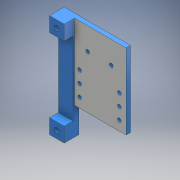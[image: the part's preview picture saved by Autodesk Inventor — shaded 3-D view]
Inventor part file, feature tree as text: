
AUTODESK INVENTOR PART (.ipt)
format: ipt  version: 2018 (Build 220112000, 112)  size: 184,832 bytes
history: native  units: mm
features: sketch x6, extrude x3, hole x3
ambient origin geometry x8: Origin, YZ Plane, XZ Plane, XY Plane, X Axis, Y Axis, Z Axis, Center Point
bodies: Solide1 (feature_tree)
feature tree (12):
  extrude  "Extrusion1"  Depth=25.0mm
  extrude  "Extrusion3"  Depth=35.0mm
  extrude  "Extrusion6"  Depth=10.0mm
  hole  "Perçage1"  [1 undecoded]
  sketch  "Esquisse9"
  hole  "Perçage2"  [1 undecoded]
  hole  "Perçage5"  [1 undecoded]
  sketch  "Esquisse1"
  sketch  "Esquisse3"
  sketch  "Esquisse7"
  sketch  "Esquisse8"
  sketch  "Esquisse18"
note: 3 required parameter values undecoded (feature->parameter linkage not recoverable at this tier; creation-order binding heuristic only, values carry confidence <= 0.55)
